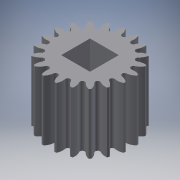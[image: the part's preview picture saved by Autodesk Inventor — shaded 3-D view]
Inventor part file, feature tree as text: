
AUTODESK INVENTOR PART (.ipt)
format: ipt  version: 2017 (Build 210142000, 142)  size: 253,440 bytes
history: native  units: mm
features: extrude x3, sketch x2, pattern_circular x1
ambient origin geometry x8: Origin, YZ Plane, XZ Plane, XY Plane, X Axis, Y Axis, Z Axis, Center Point
bodies: Solid1 (feature_tree)
feature tree (6):
  sketch  "Sketch1"  dims[d0=20.0mm d1=0.0mm]
  extrude  "Extrusion1"  TaperAngle=0.0deg  [1 undecoded]
  extrude  "Extrusion2"  Depth=9.525mm TaperAngle=360.0deg
  pattern_circular  "Circular Pattern1"  [2 undecoded]
  extrude  "Extrusion3"  Depth=9.525mm TaperAngle=0.0deg
  sketch  "Sketch2"  dims[d2=10.0mm d3=0.0mm d4=200.0mm d5=360.0deg d7=9.525mm d8=10.0mm d9=0.0mm]
note: 3 required parameter values undecoded (feature->parameter linkage not recoverable at this tier; creation-order binding heuristic only, values carry confidence <= 0.55)
